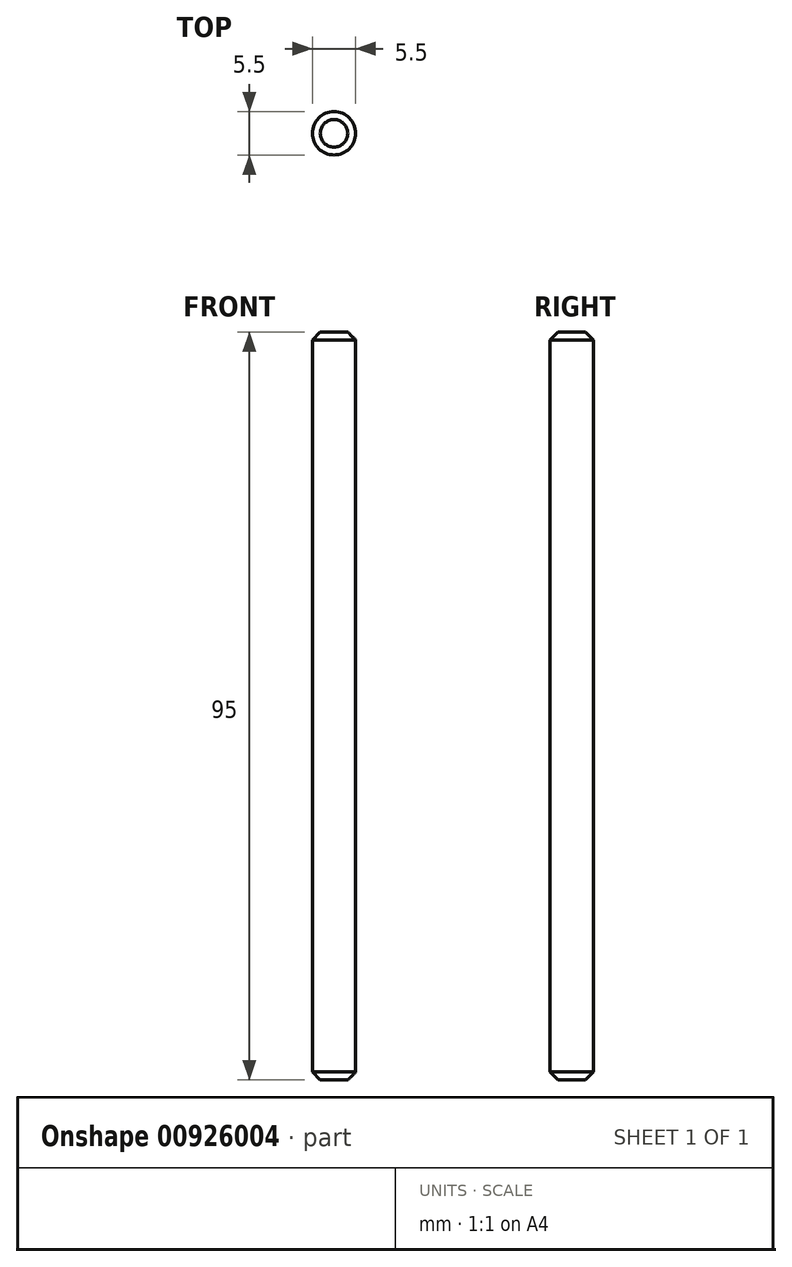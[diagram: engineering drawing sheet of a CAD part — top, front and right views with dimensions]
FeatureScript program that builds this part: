
annotation { "Feature Type Name" : "Feature", "Feature Type Description" : "" }
export const myFeature = defineFeature(function(context is Context, id is Id, definition is map)
    precondition{}
    {
        {
            var Q0;
            Q0=qCreatedBy(makeId("Top.planeOp"),FACE);
            var sketch = newSketch(context, id + "F0", { "sketchPlane" : qUnion([Q0])});
            skCircle(sketch, "E0", {"center": v(0, 0) * mm, "radius": 2.75 * mm});
            skSolve(sketch);
        }
        {
            var Q0;
            Q0=qSketchRegion(id+"F0",true);
            extrude(context, id + "F1", {"entities" : qUnion([Q0]), "endBound" : BoundingType.SYMMETRIC, "depth" : 95 * mm, "offsetDistance" : 25 * mm});
        }
        {
            var Q0;
            Q0=makeQuery(id+"F1.opExtrude","CAP_EDGE",EDGE,{"disambiguationData":[OSD([sQuery(id+"F0.wireOp",EDGE,"E0")])],"isStart":false});
            var Q1;
            Q1=makeQuery(id+"F1.opExtrude","CAP_FACE",FACE,{"disambiguationData":[OSD([sQuery(id+"F0.wireOp",EDGE,"E0")])],"isStart":true});
            chamfer(context, id + "F2", {"entities" : qUnion([Q0, Q1]), "width" : 1 * mm, "tangentPropagation" : true});
        }
    });
